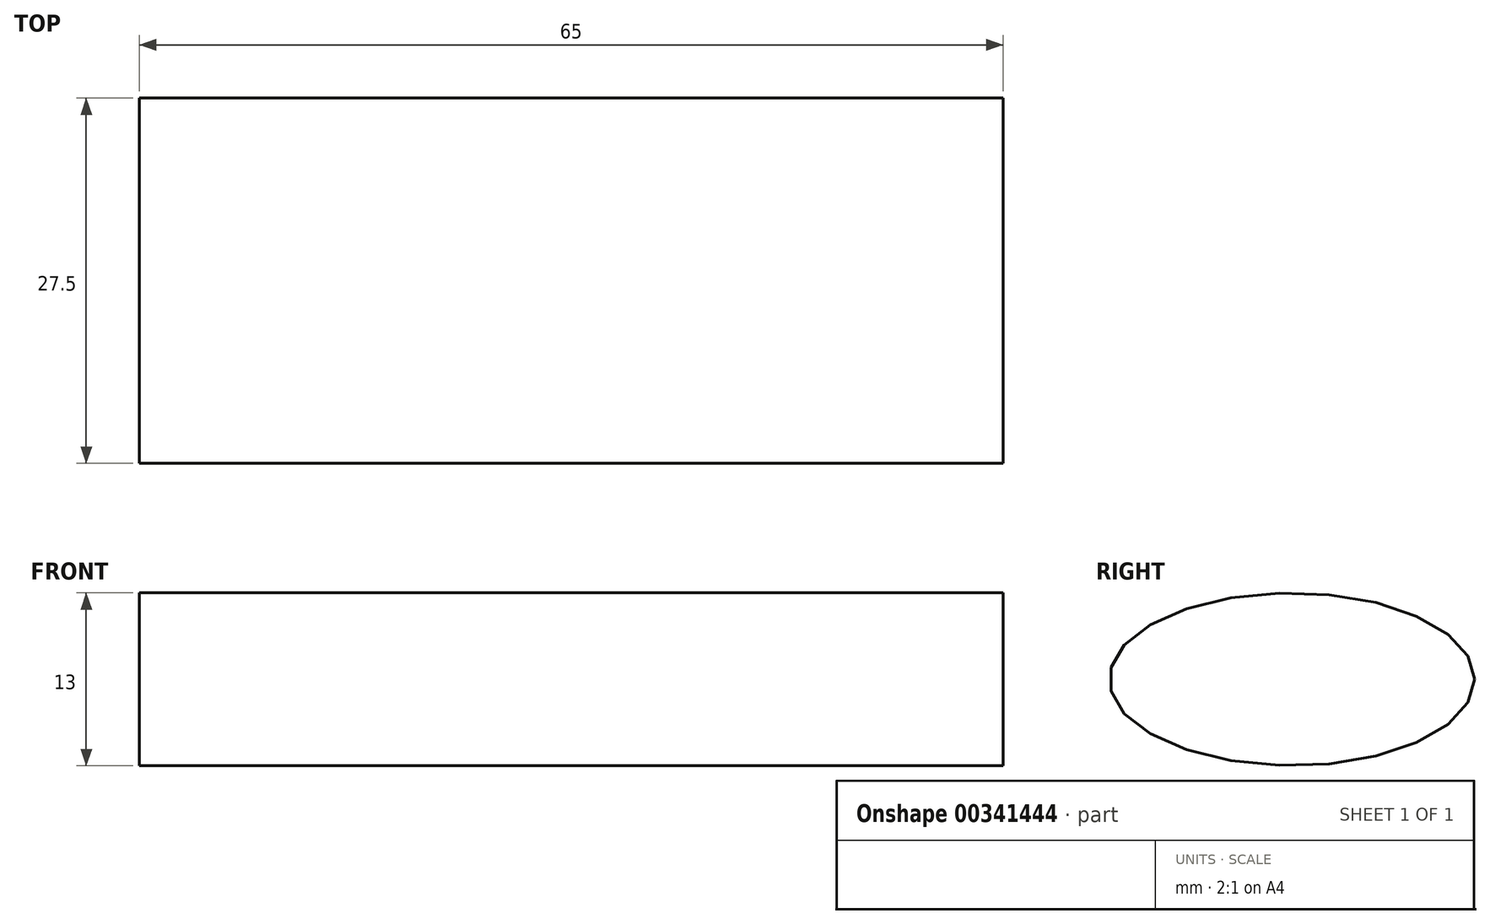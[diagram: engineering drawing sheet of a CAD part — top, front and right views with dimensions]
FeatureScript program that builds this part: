
annotation { "Feature Type Name" : "Feature", "Feature Type Description" : "" }
export const myFeature = defineFeature(function(context is Context, id is Id, definition is map)
    precondition{}
    {
        {
            var Q0;
            Q0=qCreatedBy(makeId("Right.planeOp"),FACE);
            var sketch = newSketch(context, id + "F0", { "sketchPlane" : qUnion([Q0])});
            skEllipse(sketch, "E0", {"center": v(0, 0) * mm, "majorRadius": 13.75 * mm, "minorRadius": 6.5 * mm, "majorAxis": v(1, 0)});
            skSolve(sketch);
        }
        {
            var Q0;
            Q0 = qSketchRegion(id + "F0", true);
            extrude(context, id + "F1", {"entities" : qUnion([Q0]), "depth" : 65 * mm});
        }
    });
